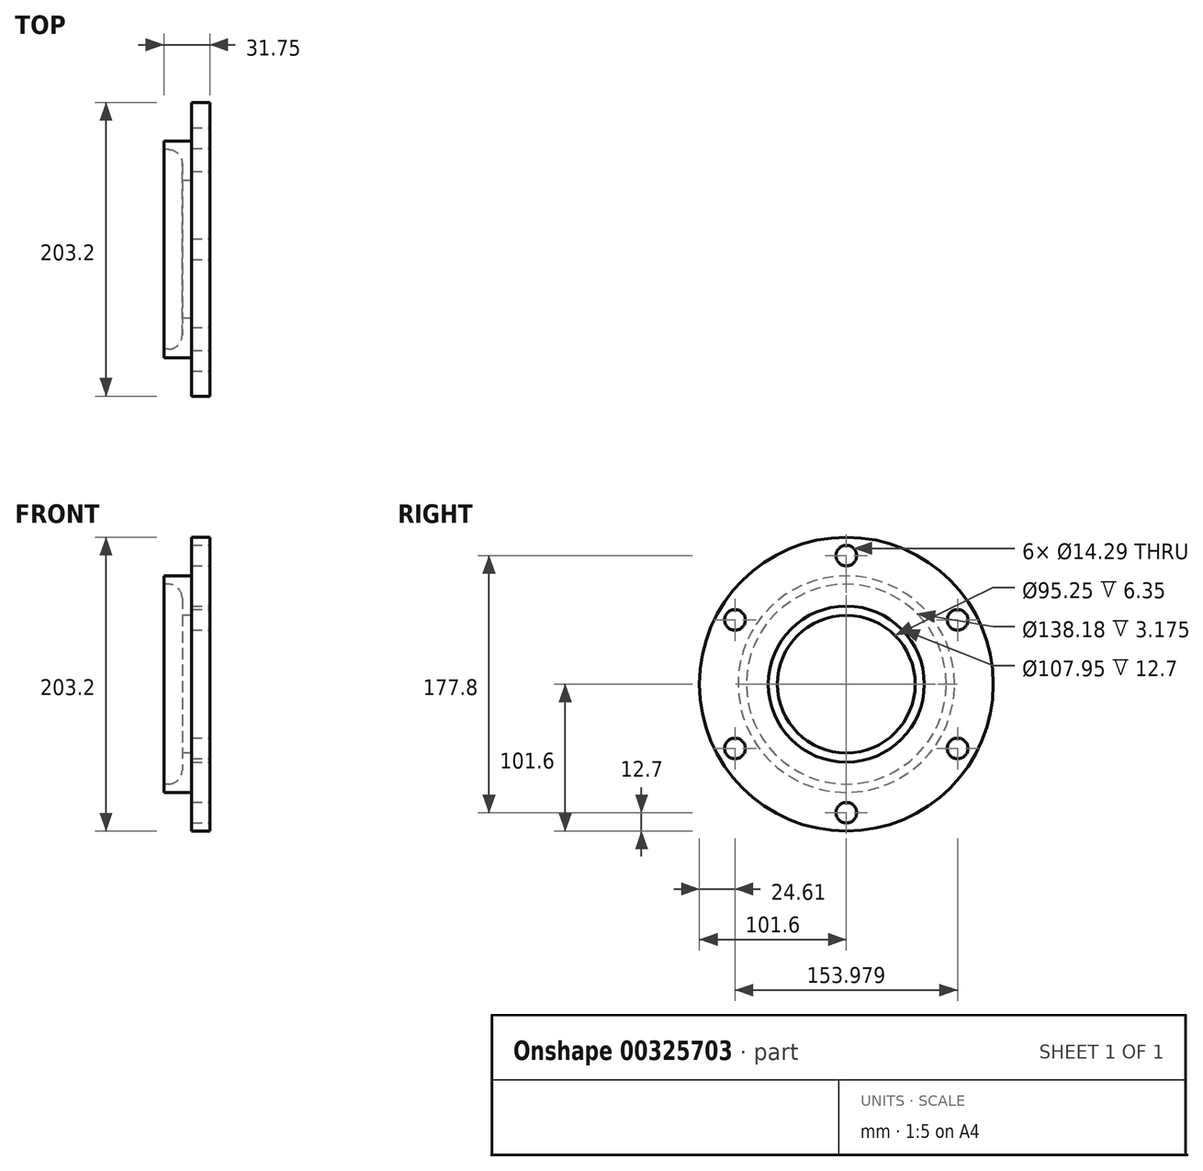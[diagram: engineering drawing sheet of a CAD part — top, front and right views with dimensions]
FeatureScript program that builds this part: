
annotation { "Feature Type Name" : "Feature", "Feature Type Description" : "" }
export const myFeature = defineFeature(function(context is Context, id is Id, definition is map)
    precondition{}
    {
        {
            var Q0;
            Q0=qCreatedBy(makeId("Right.planeOp"),FACE);
            var sketch = newSketch(context, id + "F0", { "sketchPlane" : qUnion([Q0])});
            skCircle(sketch, "E0", {"center": v(0, 0) * mm, "radius": 101.6 * mm});
            skSolve(sketch);
        }
        {
            var Q0;
            Q0=qSketchRegion(id+"F0",true);
            extrude(context, id + "F1", {"entities" : qUnion([Q0]), "depth" : 12.7 * mm});
        }
        {
            var Q0;
            Q0=makeQuery(id+"F1.opExtrude","CAP_FACE",FACE,{"disambiguationData":[OSD([sQuery(id+"F0.wireOp",EDGE,"E0")])],"isStart":true});
            var sketch = newSketch(context, id + "F2", { "sketchPlane" : qUnion([Q0])});
            skCircle(sketch, "E1", {"center": v(0, 0) * mm, "radius": 74.87 * mm});
            skSolve(sketch);
        }
        {
            var Q0;
            Q0=qSketchRegion(id+"F2",true);
            extrude(context, id + "F3", {"entities" : qUnion([Q0]), "operationType" : NewBodyOperationType.ADD, "depth" : 19.05 * mm});
        }
        {
            var Q0;
            Q0=makeQuery(id+"F3.opExtrude","CAP_FACE",FACE,{"disambiguationData":[OSD([sQuery(id+"F2.wireOp",EDGE,"E1")])],"isStart":false});
            var sketch = newSketch(context, id + "F4", { "sketchPlane" : qUnion([Q0])});
            skCircle(sketch, "E2", {"center": v(0, 0) * mm, "radius": 69.09 * mm});
            skSolve(sketch);
        }
        {
            var Q0;
            Q0=qSketchRegion(id+"F4",true);
            extrude(context, id + "F5", {"entities" : qUnion([Q0]), "operationType" : NewBodyOperationType.REMOVE, "oppositeDirection" : true, "depth" : 12.7 * mm});
        }
        {
            var Q0;
            Q0=makeQuery(id+"F5.boolean.opBoolean","COPY",EDGE,{"derivedFrom":makeQuery(id+"F5.opExtrude","CAP_EDGE",EDGE,{"disambiguationData":[OSD([sQuery(id+"F4.wireOp",EDGE,"E2")])],"isStart":false})});
            fillet(context, id + "F6", {"entities" : qUnion([Q0]), "radius" : 9.52 * mm, "tangentPropagation" : true, "allowEdgeOverflow" : false});
        }
        {
            var Q0;
            Q0=makeQuery(id+"F5.boolean.opBoolean","COPY",FACE,{"derivedFrom":makeQuery(id+"F5.opExtrude","CAP_FACE",FACE,{"disambiguationData":[OSD([sQuery(id+"F4.wireOp",EDGE,"E2")])],"isStart":false})});
            var sketch = newSketch(context, id + "F7", { "sketchPlane" : qUnion([Q0])});
            skCircle(sketch, "E3", {"center": v(0, 0) * mm, "radius": 47.63 * mm});
            skSolve(sketch);
        }
        {
            var Q0;
            Q0=qSketchRegion(id+"F7",true);
            extrude(context, id + "F8", {"entities" : qUnion([Q0]), "operationType" : NewBodyOperationType.REMOVE, "endBound" : BoundingType.THROUGH_ALL, "oppositeDirection" : true, "depth" : 25.4 * mm});
        }
        {
            var Q0;
            Q0=makeQuery(id+"F1.opExtrude","CAP_FACE",FACE,{"disambiguationData":[OSD([sQuery(id+"F0.wireOp",EDGE,"E0")])],"isStart":false});
            var sketch = newSketch(context, id + "F9", { "sketchPlane" : qUnion([Q0])});
            skCircle(sketch, "E4", {"center": v(0, 0) * mm, "radius": 53.98 * mm});
            skSolve(sketch);
        }
        {
            var Q0;
            Q0=qSketchRegion(id+"F9",true);
            extrude(context, id + "F10", {"entities" : qUnion([Q0]), "operationType" : NewBodyOperationType.REMOVE, "oppositeDirection" : true, "depth" : 12.7 * mm});
        }
        {
            var Q0;
            Q0=makeQuery(id+"F1.opExtrude","CAP_FACE",FACE,{"disambiguationData":[OSD([sQuery(id+"F0.wireOp",EDGE,"E0")])],"isStart":false});
            var sketch = newSketch(context, id + "F11", { "sketchPlane" : qUnion([Q0])});
            skCircle(sketch, "E5", {"center": v(0, 0) * mm, "radius": 88.9 * mm, "construction": true});
            skLineSegment(sketch, "E6", {"start": v(0, 0) * mm, "end": v(0, -120.17) * mm, "construction": true});
            skPoint(sketch, "E7", {"position": v(0, -88.9) * mm});
            skPoint(sketch, "E8.1.0", {"position": v(76.99, -44.45) * mm});
            skPoint(sketch, "E8.2.0", {"position": v(76.99, 44.45) * mm});
            skPoint(sketch, "E8.3.0", {"position": v(0, 88.9) * mm});
            skPoint(sketch, "E8.4.0", {"position": v(-76.99, 44.45) * mm});
            skPoint(sketch, "E8.5.0", {"position": v(-76.99, -44.45) * mm});
            skSolve(sketch);
        }
        {
            var Q0;
            Q0=sQuery(id+"F11.wireOp",VERTEX,"E7");
            var Q1;
            Q1=sQuery(id+"F11.wireOp",VERTEX,"E8.1.0");
            var Q2;
            Q2=sQuery(id+"F11.wireOp",VERTEX,"E8.2.0");
            var Q3;
            Q3=sQuery(id+"F11.wireOp",VERTEX,"E8.3.0");
            var Q4;
            Q4=sQuery(id+"F11.wireOp",VERTEX,"E8.4.0");
            var Q5;
            Q5=sQuery(id+"F11.wireOp",VERTEX,"E8.5.0");
            var Q6;
            Q6=makeQuery(id+"F1.opExtrude","SWEPT_BODY",BODY,{"disambiguationData":[OSD([sQuery(id+"F0.wireOp",EDGE,"E0")])]});
            hole(context, id + "F12", {"style" : HoleStyle.SIMPLE, "endStyle" : HoleEndStyle.THROUGH, "holeDiameter" : 14.29 * mm, "tappedDepth" : 21.59 * mm, "tapClearance" : 3, "locations" : qUnion([Q0, Q1, Q2, Q3, Q4, Q5]), "scope" : qUnion([Q6])});
        }
    });
